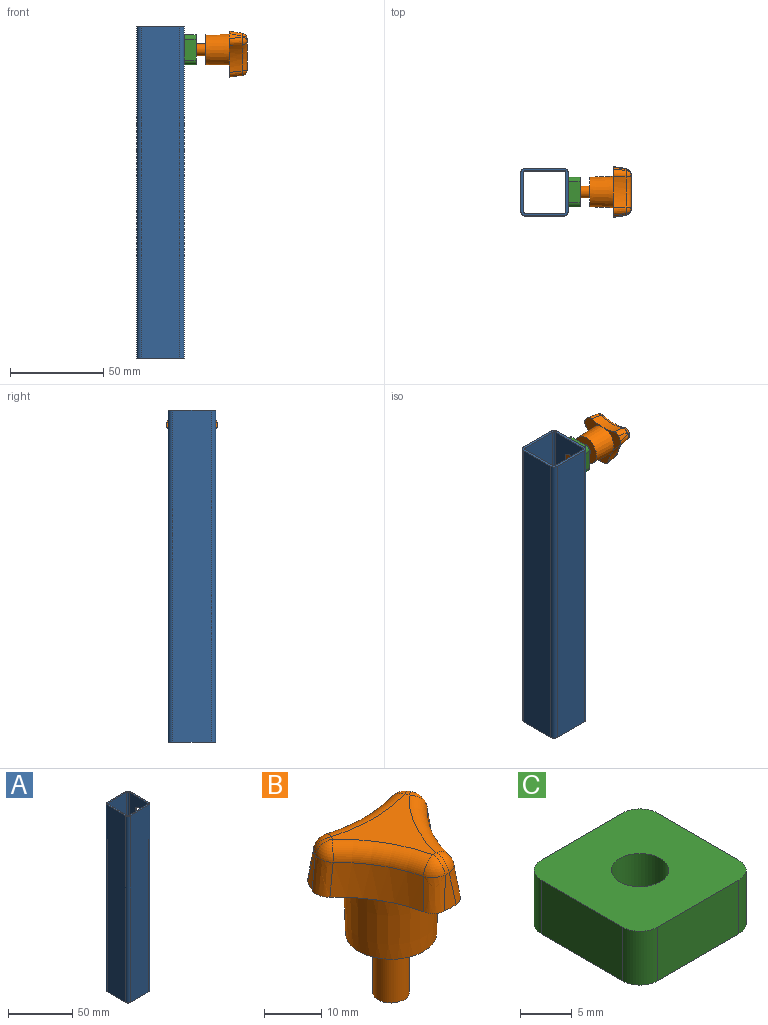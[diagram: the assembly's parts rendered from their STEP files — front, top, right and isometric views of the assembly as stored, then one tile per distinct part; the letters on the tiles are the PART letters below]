
ASSEMBLY  parts=3 mates=1
PART A: 19 faces, bbox 25.4x25.4x177.8 mm
  f0: plane 177.8x20.64mm, normal (1,0,0), area 3637.7mm2, adj f1,f15,f16,f17,f18
  f1: cylinder r=2.38mm len=177.8mm, axis (0,0,-1), area 665.1mm2, adj f0,f2,f16,f17
  f2: plane 177.8x20.64mm, normal (0,1,0), area 3669.3mm2, adj f1,f3,f16,f17
  f3: cylinder r=2.38mm len=177.8mm, axis (0,0,-1), area 665.1mm2, adj f2,f4,f16,f17
  f4: plane 177.8x20.64mm, normal (-1,0,0), area 3669.3mm2, adj f3,f5,f16,f17
  f5: cylinder r=2.38mm len=177.8mm, axis (0,0,-1), area 665.1mm2, adj f4,f6,f16,f17
  f6: plane 177.8x20.64mm, normal (0,-1,0), area 3669.3mm2, adj f5,f15,f16,f17
  f7: cylinder r=1.14mm len=177.8mm, axis (0,0,-1), area 317.5mm2, adj f8,f14,f16,f17
  f8: plane 177.8x20.64mm, normal (-1,0,0), area 3637.7mm2, adj f7,f9,f16,f17,f18
  f9: cylinder r=1.14mm len=177.8mm, axis (0,0,-1), area 317.5mm2, adj f8,f10,f16,f17
  f10: plane 177.8x20.64mm, normal (0,1,0), area 3669.3mm2, adj f9,f11,f16,f17
  f11: cylinder r=1.14mm len=177.8mm, axis (0,0,-1), area 317.5mm2, adj f10,f12,f16,f17
  f12: plane 177.8x20.64mm, normal (1,0,0), area 3669.3mm2, adj f11,f13,f16,f17
  f13: cylinder r=1.14mm len=177.8mm, axis (0,0,-1), area 317.5mm2, adj f12,f14,f16,f17
  f14: plane 177.8x20.64mm, normal (0,-1,0), area 3669.3mm2, adj f7,f13,f16,f17
  f15: cylinder r=2.38mm len=177.8mm, axis (0,0,-1), area 665.1mm2, adj f0,f6,f16,f17
  f16: plane 25.4x25.4mm, normal (0,0,1), area 116.5mm2, adj f0,f1,f2,f3,f4,f5,f6,f7
  f17: plane 25.4x25.4mm, normal (0,0,-1), area 116.5mm2, adj f0,f1,f2,f3,f4,f5,f6,f7
  f18: cylinder r=3.17mm len=6.35mm, axis (1,0,0), area 24.8mm2, adj f0,f8
PART B: 32 faces, bbox 31.2x27.4x43.1 mm
  f0: cylinder r=3.17mm len=12.7mm, axis (0,0,-1), area 253.4mm2, adj f1,f3
  f1: plane 6.35x6.35mm, normal (0,0,-1), area 31.7mm2, adj f0
  f2: cone r=7.94mm half-angle=2deg, axis (0,0,1), area 651.5mm2, adj f3,f4,f5,f13
  f3: plane 15.88x15.88mm, normal (0,0,-1), area 166.3mm2, adj f0,f2
  f4: plane 14.22x13.84mm, normal (0,0,-1), area 61.2mm2, adj f2,f6,f10,f11,f25,f31
  f5: plane 14.69x10.68mm, normal (0,0,-1), area 61.2mm2, adj f2,f6,f7,f8,f14,f19
  f6: cone r=27.64mm half-angle=7.5deg, axis (0,0,1), area 114.9mm2, adj f4,f5,f19,f24,f25
  f7: cone r=14.7mm half-angle=7.5deg, axis (0,0,-1), area 12.9mm2, adj f5,f14,f18,f19
  f8: cone r=27.64mm half-angle=7.5deg, axis (0,0,1), area 114.9mm2, adj f5,f13,f14,f16,f17
  f9: cone r=14.7mm half-angle=7.5deg, axis (0,0,-1), area 12.9mm2, adj f13,f16,f22,f23
  f10: cone r=27.64mm half-angle=7.5deg, axis (0,0,1), area 114.9mm2, adj f4,f13,f22,f28,f31
  f11: cone r=14.7mm half-angle=7.5deg, axis (0,0,-1), area 12.9mm2, adj f4,f25,f29,f31
  f12: plane 18.83x16.32mm, normal (0,0,1), area 117.9mm2, adj f17,f18,f23,f24,f28,f29
  f13: plane 14.22x13.84mm, normal (0,0,-1), area 61.2mm2, adj f2,f8,f9,f10,f16,f22
  f14: bspline ~25.75x6.02mm, area 27.6mm2, adj f5,f7,f8,f15
  f15: sphere r=3.17mm, area 6.4mm2, adj f14,f17,f18
  f16: bspline ~19.36x4.58mm, area 27.6mm2, adj f8,f9,f13,f20
  f17: torus R=31.68mm, axis (0,0,1), area 78.7mm2, adj f8,f12,f15,f20
  f18: torus R=10.66mm, axis (0,0,1), area 4.1mm2, adj f7,f12,f15,f21
  f19: bspline ~19.36x5.16mm, area 27.6mm2, adj f5,f6,f7,f21
  f20: sphere r=3.17mm, area 16mm2, adj f16,f17,f23
  f21: sphere r=3.17mm, area 17mm2, adj f18,f19,f24
  f22: bspline ~25.75x6.24mm, area 27.6mm2, adj f9,f10,f13,f26
  f23: torus R=10.66mm, axis (0,0,1), area 4.1mm2, adj f9,f12,f20,f26
  f24: torus R=31.68mm, axis (0,0,1), area 78.7mm2, adj f6,f12,f21,f27
  f25: bspline ~25.75x5.59mm, area 27.6mm2, adj f4,f6,f11,f27
  f26: sphere r=3.17mm, area 8.1mm2, adj f22,f23,f28
  f27: sphere r=3.17mm, area 6.5mm2, adj f24,f25,f29
  f28: torus R=31.68mm, axis (0,0,1), area 78.7mm2, adj f10,f12,f26,f30
  f29: torus R=10.66mm, axis (0,0,1), area 4.1mm2, adj f11,f12,f27,f30
  f30: sphere r=3.17mm, area 20.4mm2, adj f28,f29,f31
  f31: bspline ~19.36x5.07mm, area 27.6mm2, adj f4,f10,f11,f30
PART C: 11 faces, bbox 15.9x15.9x6.4 mm
  f0: plane 11.11x6.35mm, normal (1,0,0), area 70.6mm2, adj f1,f8,f9,f10
  f1: cylinder r=2.38mm len=6.35mm, axis (0,0,-1), area 23.8mm2, adj f0,f2,f9,f10
  f2: plane 11.11x6.35mm, normal (0,1,0), area 70.6mm2, adj f1,f3,f9,f10
  f3: cylinder r=2.38mm len=6.35mm, axis (0,0,-1), area 23.8mm2, adj f2,f4,f9,f10
  f4: plane 11.11x6.35mm, normal (-1,0,0), area 70.6mm2, adj f3,f5,f9,f10
  f5: cylinder r=2.38mm len=6.35mm, axis (0,0,-1), area 23.8mm2, adj f4,f6,f9,f10
  f6: plane 11.11x6.35mm, normal (0,-1,0), area 70.6mm2, adj f5,f8,f9,f10
  f7: cylinder r=2.77mm len=6.35mm, axis (0,0,-1), area 110.6mm2, adj f9,f10
  f8: cylinder r=2.38mm len=6.35mm, axis (0,0,-1), area 23.8mm2, adj f0,f6,f9,f10
  f9: plane 15.88x15.88mm, normal (0,0,1), area 223mm2, adj f0,f1,f2,f3,f4,f5,f6,f7
  f10: plane 15.88x15.88mm, normal (0,0,-1), area 223mm2, adj f0,f1,f2,f3,f4,f5,f6,f7
PLACE A at identity fixed
PLACE B rot(axis=(0.58,0.58,0.58),120deg) t=(11.46,0,165.1)mm
PLACE C rot(axis=(0.58,0.58,0.58),120deg) t=(12.7,0,165.1)mm
MATE fastened C.f7 <-> A.f18  axis (-1,0,0) through (12.7,0,165.1)mm
